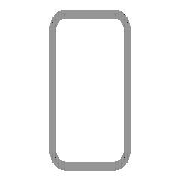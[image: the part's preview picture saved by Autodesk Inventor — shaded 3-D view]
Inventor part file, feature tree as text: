
AUTODESK INVENTOR PART (.ipt)
format: ipt  version: 2025 (Build 290162010, 162A)  size: 132,608 bytes
history: native  units: mm (DEFAULTED — no unit token found)
features: other x4, sketch x1, plane x1
ambient origin geometry x8: Origin, YZ Plane, XZ Plane, XY Plane, X Axis, Y Axis, Z Axis, Center Point
bodies: Solid1 (feature_tree), Body (feature_tree)
feature tree (6):
  parser-record x1  (decoder bookkeeping rows leaked as tree rows — omitted from the tree; the rows remain in map.json)
  other  "Driven Length"
  other  "Start Plane"
  other  "End Plane"
  sketch  "Sketch3"  dims[d3=780.0mm d4=0.0mm d7=6.0mm d9=40.0mm d11=80.0mm d12=3.0mm d13=-0.0mm d14=780.0mm d15=20.0mm d16=40.0mm d17=90.0deg d18=780.0mm]
  plane  "Work Plane3"
